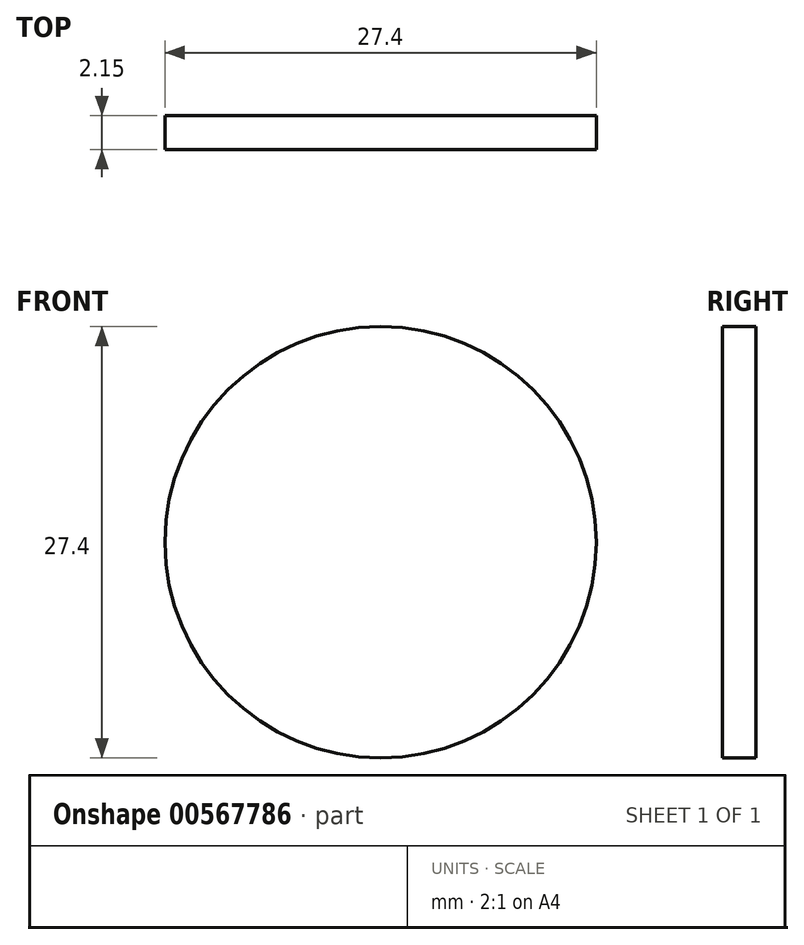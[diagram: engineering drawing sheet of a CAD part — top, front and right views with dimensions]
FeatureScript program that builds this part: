
annotation { "Feature Type Name" : "Feature", "Feature Type Description" : "" }
export const myFeature = defineFeature(function(context is Context, id is Id, definition is map)
    precondition{}
    {
        {
            var Q0;
            Q0=qCreatedBy(makeId("Front.planeOp"),FACE);
            var sketch = newSketch(context, id + "F0", { "sketchPlane" : qUnion([Q0])});
            skCircle(sketch, "E0", {"center": v(24.08, -12.8) * mm, "radius": 13.7 * mm});
            skPoint(sketch, "E1", {"position": v(24.08, 0.9) * mm});
            skPoint(sketch, "E2", {"position": v(24.08, -26.5) * mm});
            skSolve(sketch);
        }
        {
            var Q0;
            Q0 = qSketchRegion(id + "F0", true);
            extrude(context, id + "F1", {"entities" : qUnion([Q0]), "depth" : 2.15 * mm, "offsetDistance" : 25 * mm});
        }
    });
